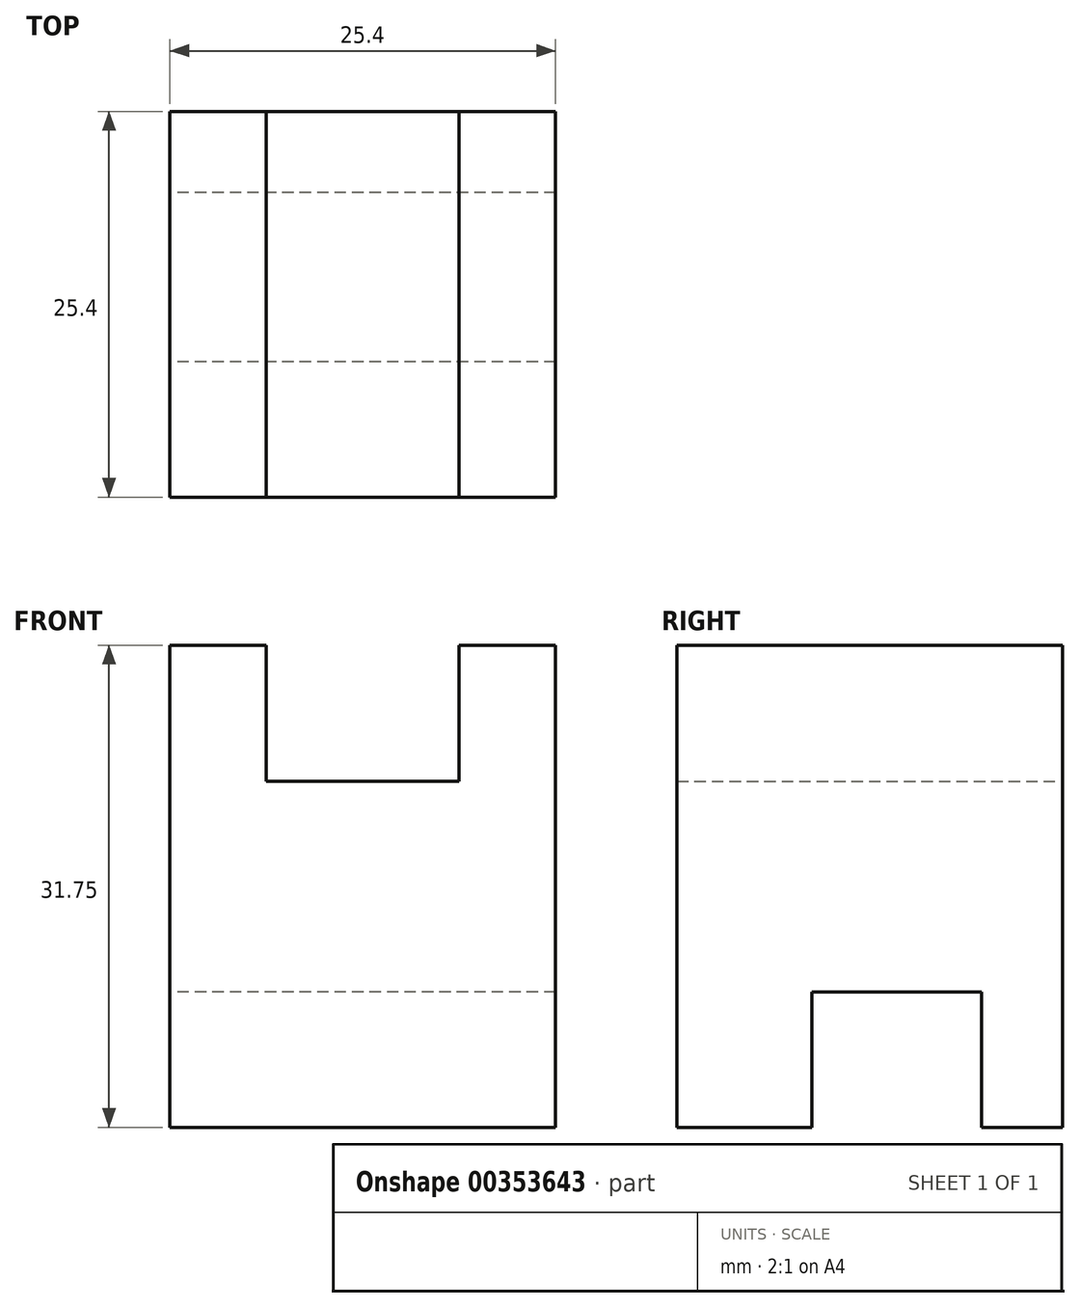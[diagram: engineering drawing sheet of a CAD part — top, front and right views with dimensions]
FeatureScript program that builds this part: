
annotation { "Feature Type Name" : "Feature", "Feature Type Description" : "" }
export const myFeature = defineFeature(function(context is Context, id is Id, definition is map)
    precondition{}
    {
        {
            var Q0;
            Q0=qCreatedBy(makeId("Front.planeOp"),FACE);
            var sketch = newSketch(context, id + "F0", { "sketchPlane" : qUnion([Q0])});
            skLineSegment(sketch, "E0", {"start": v(11.6, 0) * mm, "end": v(11.6, 31.75) * mm});
            skLineSegment(sketch, "E1", {"start": v(11.6, 31.75) * mm, "end": v(17.95, 31.75) * mm});
            skLineSegment(sketch, "E2", {"start": v(17.95, 31.75) * mm, "end": v(17.95, 22.78) * mm});
            skLineSegment(sketch, "E3", {"start": v(17.95, 22.78) * mm, "end": v(30.65, 22.78) * mm});
            skLineSegment(sketch, "E4", {"start": v(30.65, 22.78) * mm, "end": v(30.65, 31.75) * mm});
            skLineSegment(sketch, "E5", {"start": v(30.65, 31.75) * mm, "end": v(37, 31.75) * mm});
            skLineSegment(sketch, "E6", {"start": v(37, 31.75) * mm, "end": v(37, 0) * mm});
            skLineSegment(sketch, "E7", {"start": v(11.6, 0) * mm, "end": v(37, 0) * mm});
            skSolve(sketch);
        }
        {
            var Q0;
            Q0 = qSketchRegion(id + "F0", true);
            extrude(context, id + "F1", {"entities" : qUnion([Q0]), "depth" : 25.4 * mm});
        }
        {
            var Q0;
            Q0=qCreatedBy(makeId("Right.planeOp"),FACE);
            var sketch = newSketch(context, id + "F2", { "sketchPlane" : qUnion([Q0])});
            skLineSegment(sketch, "E8", {"start": v(-17.37, 0) * mm, "end": v(-17.37, 5.9) * mm});
            skLineSegment(sketch, "E9", {"start": v(-17.37, 5.9) * mm, "end": v(-7.13, 5.9) * mm});
            skLineSegment(sketch, "E10", {"start": v(-7.13, 5.9) * mm, "end": v(-7.13, 0) * mm});
            skLineSegment(sketch, "E11", {"start": v(-17.37, 0) * mm, "end": v(-7.13, 0) * mm});
            skSolve(sketch);
        }
        {
            var Q0;
            Q0 = qSketchRegion(id + "F2", true);
            extrude(context, id + "F3", {"entities" : qUnion([Q0]), "operationType" : NewBodyOperationType.REMOVE, "oppositeDirection" : true, "depth" : 12.7 * mm});
        }
        {
            var Q0;
            Q0 = qSketchRegion(id + "F2", true);
            extrude(context, id + "F4", {"entities" : qUnion([Q0]), "operationType" : NewBodyOperationType.REMOVE, "oppositeDirection" : true, "depth" : 12.7 * mm});
        }
        {
            var Q0;
            Q0=makeQuery(id+"F1.opExtrude","SWEPT_FACE",FACE,{"disambiguationData":[OSD([sQuery(id+"F0.wireOp",EDGE,"E0")])]});
            var sketch = newSketch(context, id + "F5", { "sketchPlane" : qUnion([Q0])});
            skLineSegment(sketch, "E12", {"start": v(5.33, 0) * mm, "end": v(5.33, 8.9) * mm});
            skLineSegment(sketch, "E13", {"start": v(5.33, 8.9) * mm, "end": v(16.5, 8.9) * mm});
            skLineSegment(sketch, "E14", {"start": v(16.5, 8.9) * mm, "end": v(16.5, 0) * mm});
            skLineSegment(sketch, "E15", {"start": v(16.5, 0) * mm, "end": v(5.33, 0) * mm});
            skSolve(sketch);
        }
        {
            var Q0;
            Q0 = qSketchRegion(id + "F5", true);
            extrude(context, id + "F6", {"entities" : qUnion([Q0]), "operationType" : NewBodyOperationType.REMOVE, "oppositeDirection" : true, "depth" : 25.4 * mm});
        }
    });
